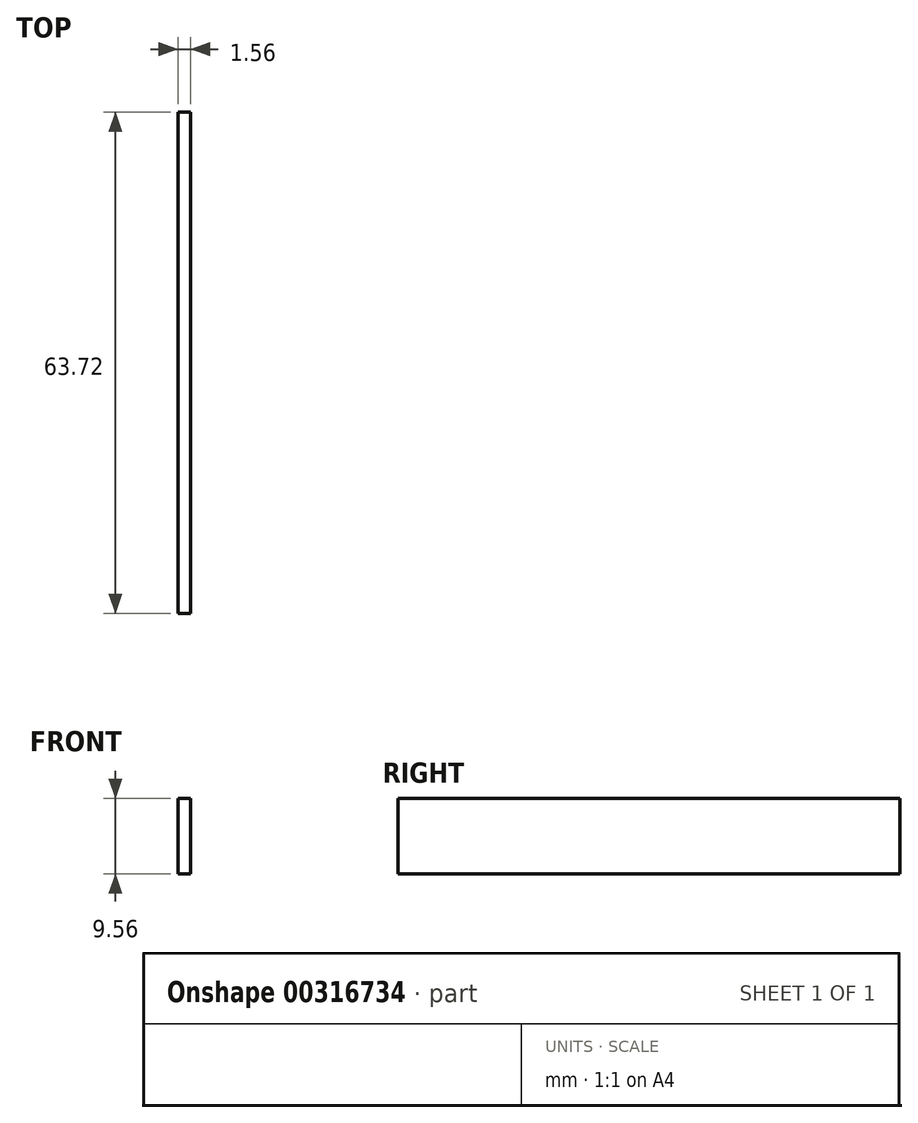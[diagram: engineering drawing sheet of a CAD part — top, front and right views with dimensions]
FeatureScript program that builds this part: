
annotation { "Feature Type Name" : "Feature", "Feature Type Description" : "" }
export const myFeature = defineFeature(function(context is Context, id is Id, definition is map)
    precondition{}
    {
        {
            var Q0;
            Q0=qCreatedBy(makeId("Right.planeOp"),FACE);
            var sketch = newSketch(context, id + "F0", { "sketchPlane" : qUnion([Q0])});
            skLineSegment(sketch, "E0", {"start": v(-10.91, 7.92) * mm, "end": v(-10.91, -1.64) * mm});
            skLineSegment(sketch, "E1", {"start": v(-10.91, -1.64) * mm, "end": v(52.8, -1.64) * mm});
            skLineSegment(sketch, "E2", {"start": v(52.8, -1.64) * mm, "end": v(52.8, 7.92) * mm});
            skLineSegment(sketch, "E3", {"start": v(52.8, 7.92) * mm, "end": v(-10.91, 7.92) * mm});
            skSolve(sketch);
        }
        {
            var Q0;
            Q0 = qSketchRegion(id + "F0", true);
            extrude(context, id + "F1", {"entities" : qUnion([Q0]), "depth" : 1.56 * mm});
        }
    });
